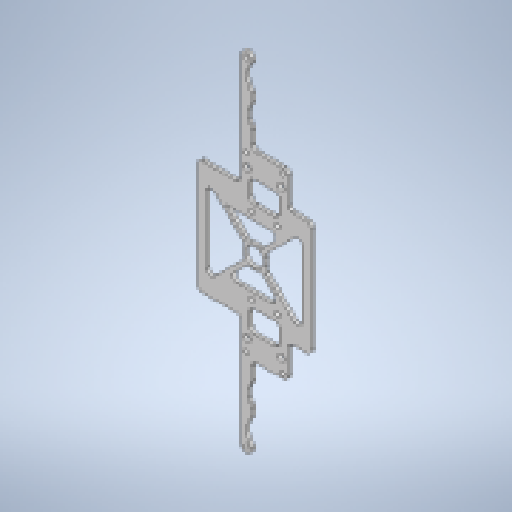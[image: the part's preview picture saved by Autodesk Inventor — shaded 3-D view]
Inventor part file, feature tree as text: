
AUTODESK INVENTOR PART (.ipt)
format: ipt  version: 2025.1 (Build 291241000, 241)  size: 637,440 bytes
history: native  units: mm
features: reference x11, extrude x9, sketch x9, other x8, fillet x6, projected_geometry x1
ambient origin geometry x8: Origin, YZ Plane, XZ Plane, XY Plane, X Axis, Y Axis, Z Axis, Center Point
bodies: Body1 (feature_tree)
feature tree (44):
  other  "ソリッド1"
  extrude  "押し出し1"  Depth=2.2mm
  extrude  "押し出し2"  Depth=2.2mm
  extrude  "押し出し3"  Depth=2.2mm
  fillet  "フィレット1"  Radius=21.0mm
  extrude  "押し出し4"  Depth=80.0mm
  fillet  "フィレット2"  Radius=1.5mm
  extrude  "押し出し6"  Depth=2.2mm
  extrude  "押し出し7"  Depth=2.2mm
  fillet  "フィレット4"  Radius=2.2mm
  fillet  "フィレット5"  Radius=16.0mm
  extrude  "押し出し8"  Depth=8.0mm
  extrude  "押し出し9"  Depth=2.0mm
  fillet  "フィレット6"  [1 undecoded]
  extrude  "押し出し10"  Depth=11.0mm
  fillet  "フィレット7"  Radius=33.5mm
  sketch  "スケッチ1"
  sketch  "スケッチ2"
  sketch  "スケッチ3"
  reference  "参照3"
  reference  "参照4"
  reference  "参照5"
  reference  "参照6"
  sketch  "スケッチ4"
  reference  "参照7"
  reference  "参照8"
  reference  "参照9"
  reference  "参照10"
  sketch  "スケッチ6"
  sketch  "スケッチ7"
  reference  "参照11"
  sketch  "スケッチ8"
  reference  "参照12"
  reference  "参照13"
  sketch  "スケッチ9"
  projected_geometry  "投影ループ1"
  sketch  "スケッチ10"
  other  "<userpath>\Documents\Inventor\Vixen\doutai.iam"
  other  "doutai.iam"
  other  "KRS2500_scale:6"
  other  "02157_SmallDiameterHornB:4"
  other  "02157_SmallDiameterHornB:5"
  other  "KRS2500_scale:5"
  other  "kataue:1"
note: 1 required parameter value undecoded (feature->parameter linkage not recoverable at this tier; creation-order binding heuristic only, values carry confidence <= 0.55)
